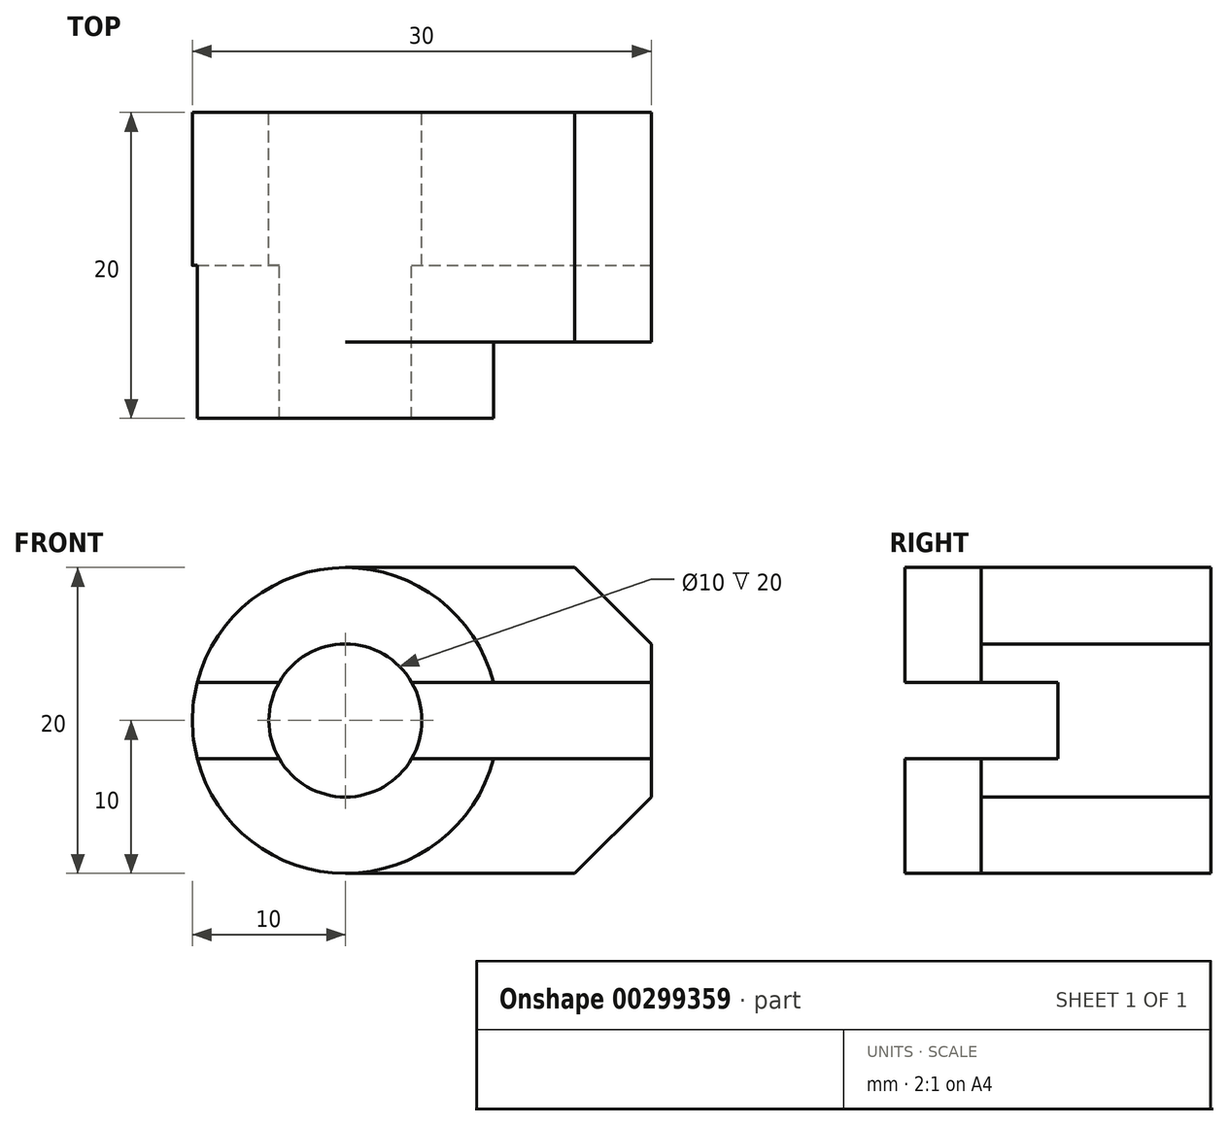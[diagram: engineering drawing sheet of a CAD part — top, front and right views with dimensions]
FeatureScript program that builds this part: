
annotation { "Feature Type Name" : "Feature", "Feature Type Description" : "" }
export const myFeature = defineFeature(function(context is Context, id is Id, definition is map)
    precondition{}
    {
        {
            var Q0;
            Q0=qCreatedBy(makeId("Front.planeOp"),FACE);
            var sketch = newSketch(context, id + "F0", { "sketchPlane" : qUnion([Q0])});
            skCircle(sketch, "E0", {"center": v(0, 0) * mm, "radius": 5 * mm});
            skCircle(sketch, "E1", {"center": v(0, 0) * mm, "radius": 10 * mm});
            skLineSegment(sketch, "E2", {"start": v(0, 10) * mm, "end": v(15, 10) * mm});
            skLineSegment(sketch, "E3", {"start": v(15, 10) * mm, "end": v(20, 5) * mm});
            skLineSegment(sketch, "E4", {"start": v(20, 5) * mm, "end": v(20, -5) * mm});
            skLineSegment(sketch, "E5", {"start": v(0, -10) * mm, "end": v(15, -10) * mm});
            skLineSegment(sketch, "E6", {"start": v(15, -10) * mm, "end": v(20, -5) * mm});
            skSolve(sketch);
        }
        {
            var Q0;
            Q0 = qSketchRegion(id + "F0", true);
            extrude(context, id + "F1", {"entities" : qUnion([Q0]), "depth" : 15 * mm});
        }
        {
            var Q0;
            Q0=makeQuery(id+"F1.opExtrude","CAP_FACE",FACE,{"disambiguationData":[OSD([sQuery(id+"F0.wireOp",EDGE,"E0"),sQuery(id+"F0.wireOp",EDGE,"E1"),sQuery(id+"F0.wireOp",EDGE,"E2"),sQuery(id+"F0.wireOp",EDGE,"E3"),sQuery(id+"F0.wireOp",EDGE,"E4"),sQuery(id+"F0.wireOp",EDGE,"E5"),sQuery(id+"F0.wireOp",EDGE,"E6")])],"isStart":false});
            var sketch = newSketch(context, id + "F2", { "sketchPlane" : qUnion([Q0])});
            skCircle(sketch, "E7", {"center": v(0, 0) * mm, "radius": 5 * mm});
            skCircle(sketch, "E8", {"center": v(0, 0) * mm, "radius": 10 * mm});
            skSolve(sketch);
        }
        {
            var Q0;
            Q0 = qSketchRegion(id + "F2", true);
            extrude(context, id + "F3", {"entities" : qUnion([Q0]), "operationType" : NewBodyOperationType.ADD, "depth" : 5 * mm});
        }
        {
            var Q0;
            Q0=makeQuery(id+"F1.opExtrude","SWEPT_FACE",FACE,{"disambiguationData":[OSD([sQuery(id+"F0.wireOp",EDGE,"E4")])]});
            var sketch = newSketch(context, id + "F4", { "sketchPlane" : qUnion([Q0])});
            skLineSegment(sketch, "E9.bottom", {"start": v(-20, 2.5) * mm, "end": v(-10, 2.5) * mm});
            skLineSegment(sketch, "E9.top", {"start": v(-20, -2.5) * mm, "end": v(-10, -2.5) * mm});
            skLineSegment(sketch, "E9.left", {"start": v(-20, 2.5) * mm, "end": v(-20, -2.5) * mm});
            skLineSegment(sketch, "E9.right", {"start": v(-10, 2.5) * mm, "end": v(-10, -2.5) * mm});
            skSolve(sketch);
        }
        {
            var Q0;
            Q0 = qSketchRegion(id + "F4", true);
            extrude(context, id + "F5", {"entities" : qUnion([Q0]), "operationType" : NewBodyOperationType.REMOVE, "endBound" : BoundingType.THROUGH_ALL, "oppositeDirection" : true, "depth" : 25 * mm});
        }
    });
